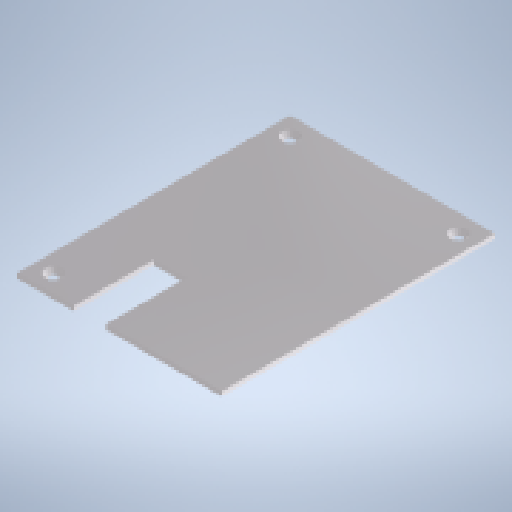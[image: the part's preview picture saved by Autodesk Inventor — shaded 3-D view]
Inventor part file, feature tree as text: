
AUTODESK INVENTOR PART (.ipt)
format: ipt  version: 2025 (Build 290162010, 162A)  size: 174,080 bytes
history: native  units: mm
features: sketch x2, extrude x1, hole x1, other x1
ambient origin geometry x8: Origin, YZ Plane, XZ Plane, XY Plane, X Axis, Y Axis, Z Axis, Center Point
bodies: Volumenkörper1 (feature_tree)
feature tree (5):
  extrude  "Extrusion1"  Depth=35.0mm
  hole  "Bohrung1"  [1 undecoded]
  sketch  "Skizze1"  dims[d0=14.0mm d1=35.0mm]
  sketch  "Skizze2"  dims[d2=25.0mm d3=0.0mm d4=0.0mm d5=8.0mm d6=8.0mm d7=8.0mm d8=8.0mm d9=3.4mm d10=6.0mm d11=6.3mm d12=2.0mm d13=90.0deg d14=8.0mm d15=20.594885mm]
  other  "item_47308_blech-al-2mm-naturfarben_120_90_high_1_1:1"
note: 1 required parameter value undecoded (feature->parameter linkage not recoverable at this tier; creation-order binding heuristic only, values carry confidence <= 0.55)
